# Revit family: Window-Fixed_Kawneer_8410TL-01_21020
name_source: partatom
category: Windows
revit_build: Autodesk Revit Architecture 2013 (Build: 20120221_2030(x64)
units: mm (PartAtom-declared; Revit-internal decimal feet)

## types (1)
- Window-Fixed_Kawneer_8410TL-01_21020
    2- and 4-Sided Structural Glazed = No
    CSI Masterformat Code = 08 51 13
    Color = any
    Default Sill Height = 31 1/2"
    Depth = 4"
    Description = Heavy Commercial and Architectural Window Grade window with a variety of operating functions. Suitable for any building application from low to high rise including new and remodel construction. Tested to both HC  nd AW high performance standards. Available  with the patented ISOLOCK® polyurethane thermal break for insulating glass.
    Design Pressure = Fixed  F-HC100 / F-AW100
Single Hung H-HC70 / H-AW70
Double Hung H-HC70 / H-AW70
Horizontal Slider HS-HC70 / HS-AW70
    Frame Material = Aluminum - ASTM B 221 - 6063-T6 alloy and temper
    Function (Interior or Exterior) = Exterior, Interior
    Glass U-Factor = Fixed 0.48 to 0.24
    Glazing Thickness = 1/4"
    Height = 72"
    Hurricane Resistant Tested = Product tested Small and Large Missile
    Keywords = Single Hung, Double Hung and sliding.
    Manufacturer = Kawneer
    Manufacturer Part Number = 8400TL ISOLOCK® Window
    Maximum Height = 0"
    Maximum Width = 0"
    Minimum Height = 0"
    Minimum Width = 0"
    Model = 8400TL ISOLOCK® Window
    Outside Glazed = No
    Overall U-Factor = Single Hung 0.51
Double Hung 0.52
Slider 0.55
    Short Description = Sliding/Hung Window
    Style = Single Hung
Double Hung
Slider
    Subcategory = Single Hung
    Type Comments = 4" Thermal Heavy Commercial Window and Architectural Window
    Type of Glazing = monolithic, insulating
    URL = http://www.kawneer.com
    Wall Closure = By host
    Width = 60"
    Window Pane = Glass
    ecoScorecard Product Page = http://kawneer.ecoscorecard.com
    ecoScorecard_data = http://products.ecoscorecard.com

## geometry (parser evidence)
native form markers: Sweep x2
no freeform markers — native parametric forms only
